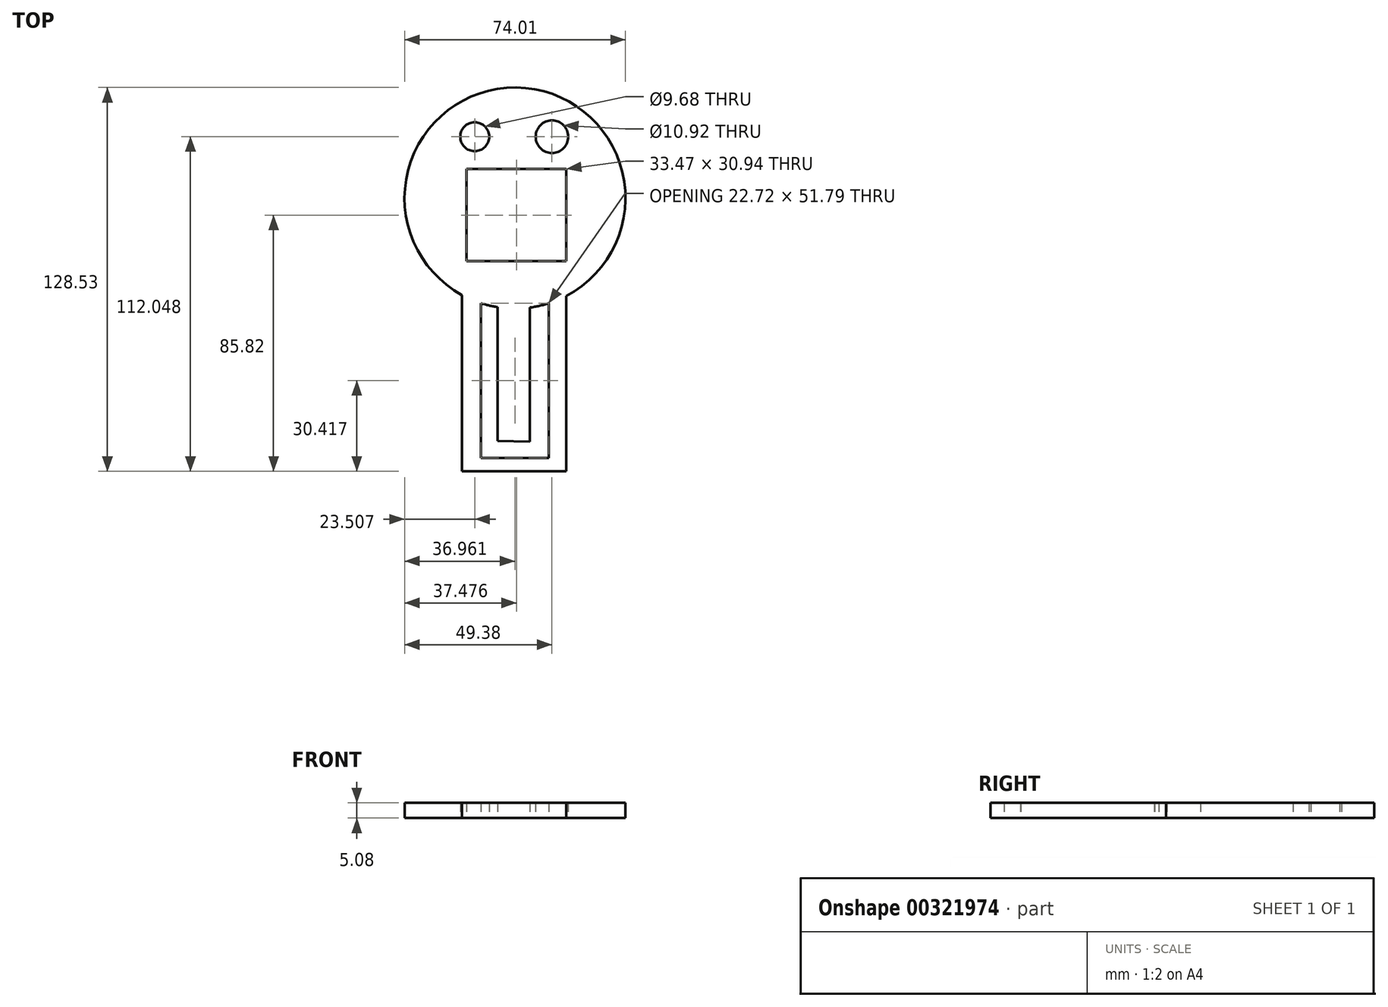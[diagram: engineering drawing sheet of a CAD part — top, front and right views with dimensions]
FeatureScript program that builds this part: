
annotation { "Feature Type Name" : "Feature", "Feature Type Description" : "" }
export const myFeature = defineFeature(function(context is Context, id is Id, definition is map)
    precondition{}
    {
        {
            var Q0;
            Q0=qCreatedBy(makeId("Top.planeOp"),FACE);
            var sketch = newSketch(context, id + "F0", { "sketchPlane" : qUnion([Q0])});
            skCircle(sketch, "E0", {"center": v(0.8, 30.87) * mm, "radius": 37 * mm});
            skCircle(sketch, "E1", {"center": v(-12.7, 51.4) * mm, "radius": 4.84 * mm});
            skCircle(sketch, "E2", {"center": v(13.17, 51.4) * mm, "radius": 5.46 * mm});
            skLineSegment(sketch, "E3", {"start": v(5.76, -5.8) * mm, "end": v(5.76, -50.69) * mm});
            skLineSegment(sketch, "E4.bottom", {"start": v(-15.47, 40.64) * mm, "end": v(18, 40.64) * mm});
            skLineSegment(sketch, "E4.top", {"start": v(-15.47, 9.7) * mm, "end": v(18, 9.7) * mm});
            skLineSegment(sketch, "E4.left", {"start": v(-15.47, 40.64) * mm, "end": v(-15.47, 9.7) * mm});
            skLineSegment(sketch, "E4.right", {"start": v(18, 40.64) * mm, "end": v(18, 9.7) * mm});
            skLineSegment(sketch, "E5", {"start": v(-5.09, -5.67) * mm, "end": v(-5.09, -50.48) * mm});
            skLineSegment(sketch, "E6", {"start": v(-5.09, -50.48) * mm, "end": v(8.44, -50.69) * mm});
            skLineSegment(sketch, "E7", {"start": v(-10.6, -4.34) * mm, "end": v(-10.6, -50.48) * mm});
            skLineSegment(sketch, "E8", {"start": v(-10.6, -50.48) * mm, "end": v(-10.6, -56.13) * mm});
            skLineSegment(sketch, "E9", {"start": v(-10.6, -56.13) * mm, "end": v(12.1, -56.13) * mm});
            skLineSegment(sketch, "E10", {"start": v(12.1, -56.13) * mm, "end": v(12.1, -4.37) * mm});
            skLineSegment(sketch, "E11", {"start": v(-16.93, -1.62) * mm, "end": v(-16.93, -58.9) * mm});
            skLineSegment(sketch, "E12", {"start": v(-16.93, -60.65) * mm, "end": v(17.9, -60.65) * mm});
            skLineSegment(sketch, "E13", {"start": v(17.9, -60.65) * mm, "end": v(17.9, -1.95) * mm});
            skLineSegment(sketch, "E14", {"start": v(17.9, -1.95) * mm, "end": v(-16.93, -1.62) * mm});
            skLineSegment(sketch, "E15", {"start": v(-16.93, -58.9) * mm, "end": v(-16.93, -60.65) * mm});
            skSolve(sketch);
        }
        {
            var Q0;
            Q0=makeQuery(id+"F0.imprint","IMPRINT",FACE,{"disambiguationData":[TD([[makeQuery(id+"F0.imprint","IMPRINT",EDGE,{"derivedFrom":sQuery(id+"F0.wireOp",EDGE,"E1")}),-1.0]])]});
            var Q1;
            {var subQ4=sQuery(id+"F0.wireOp",EDGE,"E7");Q1=makeQuery(id+"F0.imprint","IMPRINT",FACE,{"disambiguationData":[TD([[makeQuery(id+"F0.imprint","IMPRINT",EDGE,{"derivedFrom":subQ4}),-1.0]])]});}
            var Q2;
            {var subQ5=sQuery(id+"F0.wireOp",EDGE,"E14");Q2=makeQuery(id+"F0.imprint","IMPRINT",FACE,{"disambiguationData":[TD([[makeQuery(id+"F0.imprint","IMPRINT",EDGE,{"derivedFrom":subQ5}),1.0]])]});}
            var Q3;
            {var subQ3=sQuery(id+"F0.wireOp",EDGE,"E5");Q3=makeQuery(id+"F0.imprint","IMPRINT",FACE,{"disambiguationData":[TD([[makeQuery(id+"F0.imprint","IMPRINT",EDGE,{"derivedFrom":subQ3}),1.0]])]});}
            extrude(context, id + "F1", {"entities" : qUnion([Q0, Q1, Q2, Q3]), "depth" : 5.08 * mm});
        }
    });
